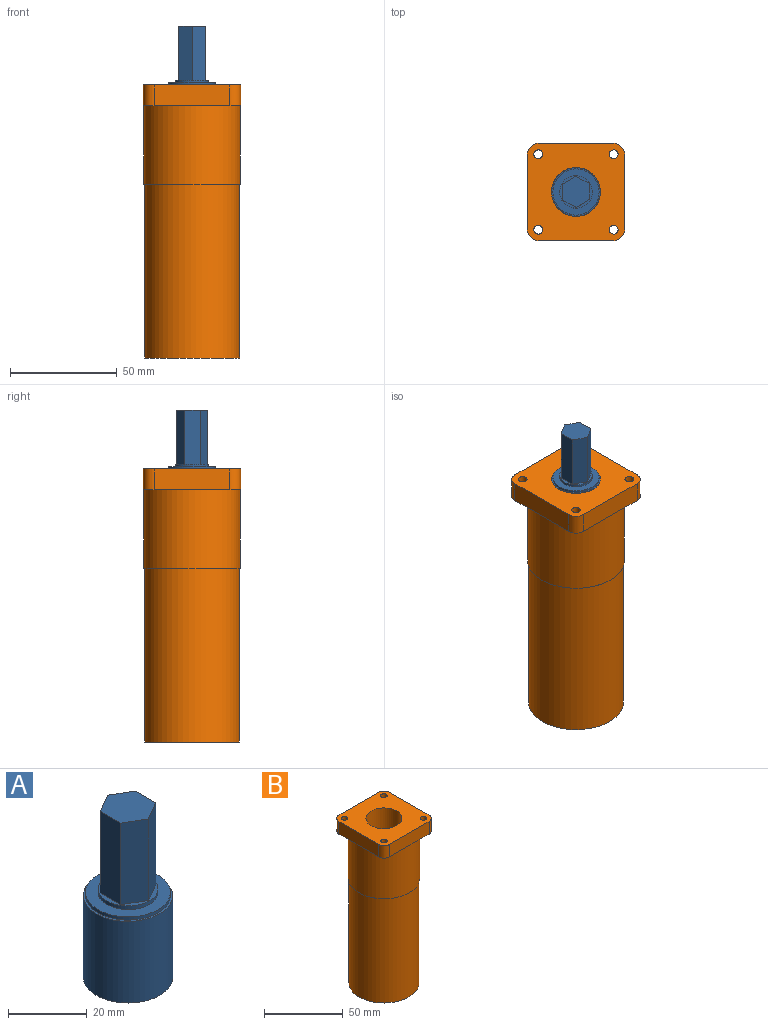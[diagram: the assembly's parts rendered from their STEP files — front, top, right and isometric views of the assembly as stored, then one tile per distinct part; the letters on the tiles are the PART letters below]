
ASSEMBLY  parts=2 mates=1
PART A: 14 faces, bbox 22.7x22.7x53 mm
  f0: cylinder r=11.37mm len=25.4mm, axis (0,0,-1), area 1814mm2, adj f1,f2
  f1: plane 22.73x22.73mm, normal (0,0,1), area 39.8mm2, adj f0,f3
  f2: plane 22.73x22.73mm, normal (0,0,-1), area 405.9mm2, adj f0
  f3: cylinder r=10.79mm len=21.59mm, axis (0,0,-1), area 68.9mm2, adj f1,f4
  f4: plane 21.59x21.59mm, normal (0,0,1), area 183.7mm2, adj f3,f5
  f5: cylinder r=7.62mm len=15.24mm, axis (0,0,-1), area 54.7mm2, adj f4,f6
  f6: plane 15.24x15.24mm, normal (0,0,1), area 42.7mm2, adj f5,f7,f8,f9,f10,f11,f12
  f7: plane 25.4x6.35mm, normal (-0.5,-0.87,0), area 186.2mm2, adj f6,f8,f12,f13
  f8: plane 25.4x6.35mm, normal (0.5,-0.87,0), area 186.2mm2, adj f6,f7,f9,f13
  f9: plane 25.4x7.33mm, normal (1,0,0), area 186.2mm2, adj f6,f8,f10,f13
  f10: plane 25.4x6.35mm, normal (0.5,0.87,0), area 186.2mm2, adj f6,f9,f11,f13
  f11: plane 25.4x6.35mm, normal (-0.5,0.87,0), area 186.2mm2, adj f6,f10,f12,f13
  f12: plane 25.4x7.33mm, normal (-1,0,0), area 186.2mm2, adj f6,f7,f11,f13
  f13: plane 14.66x12.7mm, normal (0,0,1), area 139.7mm2, adj f7,f8,f9,f10,f11,f12
PART B: 20 faces, bbox 45.5x45.5x127.8 mm
  f0: cylinder r=22.23mm len=81.28mm, axis (0,0,-1), area 11350.2mm2, adj f1,f3
  f1: plane 44.45x44.45mm, normal (0,0,-1), area 1551.8mm2, adj f0
  f2: cylinder r=22.61mm len=45.21mm, axis (0,0,-1), area 5231.2mm2, adj f3,f9
  f3: plane 45.21x45.21mm, normal (0,0,-1), area 53.7mm2, adj f0,f2
  f4: plane 35.31x9.65mm, normal (0,1,0), area 340.8mm2, adj f8,f9,f10,f13
  f5: plane 35.31x9.65mm, normal (-1,0,0), area 340.8mm2, adj f8,f9,f10,f11
  f6: plane 35.31x9.65mm, normal (0,-1,0), area 340.8mm2, adj f8,f9,f11,f12
  f7: plane 35.31x9.65mm, normal (1,0,0), area 340.8mm2, adj f8,f9,f12,f13
  f8: plane 45.47x45.47mm, normal (0,0,1), area 1581.4mm2, adj f4,f5,f6,f7,f10,f11,f12,f13
  f9: plane 45.47x45.47mm, normal (0,0,-1), area 386.4mm2, adj f2,f4,f5,f6,f7,f10,f11,f12
  f10: cylinder r=5.08mm len=9.65mm, axis (0,0,1), area 77mm2, adj f4,f5,f8,f9
  f11: cylinder r=5.08mm len=9.65mm, axis (0,0,-1), area 77mm2, adj f5,f6,f8,f9
  f12: cylinder r=5.08mm len=9.65mm, axis (0,0,1), area 77mm2, adj f6,f7,f8,f9
  f13: cylinder r=5.08mm len=9.65mm, axis (0,0,-1), area 77mm2, adj f4,f7,f8,f9
  f14: cylinder r=2.06mm len=9.65mm, axis (0,0,1), area 124.8mm2, adj f8,f9
  f15: cylinder r=2.06mm len=9.65mm, axis (0,0,1), area 124.8mm2, adj f8,f9
  f16: cylinder r=2.06mm len=9.65mm, axis (0,0,1), area 124.8mm2, adj f8,f9
  f17: cylinder r=2.06mm len=9.65mm, axis (0,0,1), area 124.8mm2, adj f8,f9
  f18: cylinder r=11.43mm len=25.4mm, axis (0,0,1), area 1824.1mm2, adj f8,f19
  f19: plane 22.86x22.86mm, normal (0,0,1), area 410.4mm2, adj f18
PLACE A rot(axis=(0,0,-1),58deg) t=(-29.67,7.5,75.43)mm
PLACE B t=(-29.67,7.5,-26.93)mm fixed
MATE revolute A.f0 <-> B.f18  axis (0,0,-1) through (-29.67,7.5,100.83)mm
